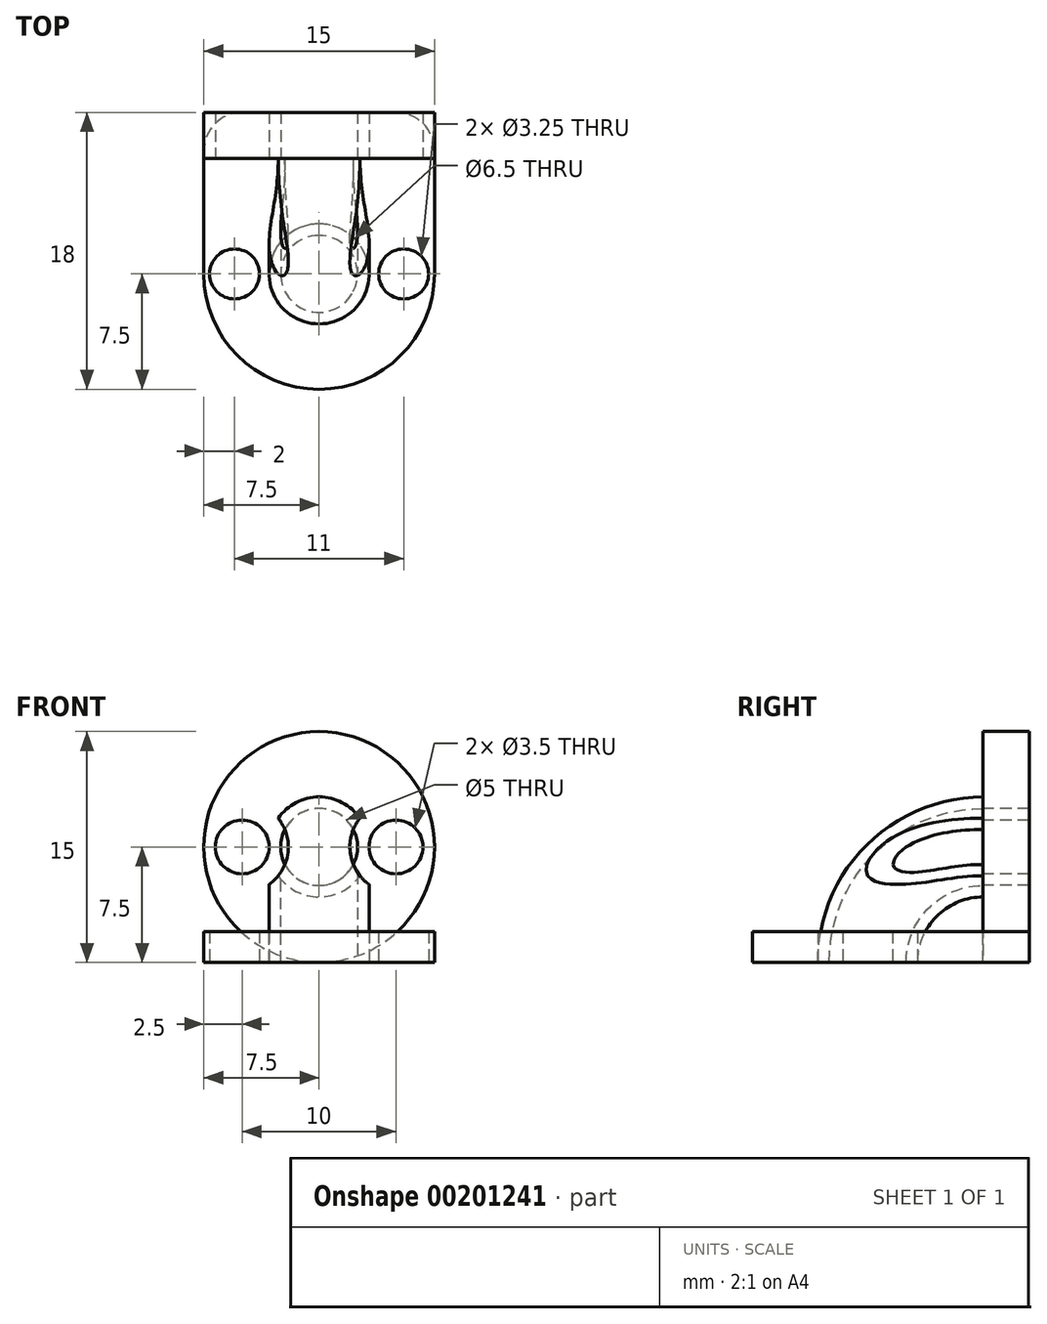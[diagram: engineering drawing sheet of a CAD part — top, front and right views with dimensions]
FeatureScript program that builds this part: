
annotation { "Feature Type Name" : "Feature", "Feature Type Description" : "" }
export const myFeature = defineFeature(function(context is Context, id is Id, definition is map)
    precondition{}
    {
        {
            var Q0;
            Q0=qCreatedBy(makeId("Front.planeOp"),FACE);
            var sketch = newSketch(context, id + "F0", { "sketchPlane" : qUnion([Q0])});
            skCircle(sketch, "E0", {"center": v(0, 0) * mm, "radius": 7.5 * mm});
            skCircle(sketch, "E1", {"center": v(0, 0) * mm, "radius": 2.5 * mm});
            skSolve(sketch);
        }
        {
            var Q0;
            Q0=qSketchRegion(id+"F0",true);
            extrude(context, id + "F1", {"entities" : qUnion([Q0]), "oppositeDirection" : true, "depth" : 3 * mm});
        }
        {
            var Q0;
            Q0=makeQuery(id+"F1.opExtrude","CAP_FACE",FACE,{"disambiguationData":[OSD([sQuery(id+"F0.wireOp",EDGE,"E0"),sQuery(id+"F0.wireOp",EDGE,"E1")])],"isStart":true});
            var sketch = newSketch(context, id + "F2", { "sketchPlane" : qUnion([Q0])});
            skPoint(sketch, "E2", {"position": v(5, 0) * mm});
            skPoint(sketch, "E3", {"position": v(-5, 0) * mm});
            skCircle(sketch, "E4", {"center": v(5, 0) * mm, "radius": 1.75 * mm});
            skCircle(sketch, "E5", {"center": v(-5, 0) * mm, "radius": 1.75 * mm});
            skSolve(sketch);
        }
        {
            var Q0;
            Q0=qSketchRegion(id+"F2",true);
            extrude(context, id + "F3", {"entities" : qUnion([Q0]), "operationType" : NewBodyOperationType.REMOVE, "oppositeDirection" : true, "depth" : 25 * mm});
        }
        {
            var Q0;
            Q0=qCreatedBy(makeId("Right.planeOp"),FACE);
            var sketch = newSketch(context, id + "F4", { "sketchPlane" : qUnion([Q0])});
            skPoint(sketch, "E6", {"position": v(0, -7.5) * mm});
            skArc(sketch, "E7", {"start": v(0, 0) * mm, "mid": v(-5.3, -2.2) * mm, "end": v(-7.5, -7.5) * mm});
            skSolve(sketch);
        }
        {
            var Q0;
            Q0=qCreatedBy(makeId("Front.planeOp"),FACE);
            var sketch = newSketch(context, id + "F5", { "sketchPlane" : qUnion([Q0])});
            skCircle(sketch, "E8", {"center": v(0, 0) * mm, "radius": 2.5 * mm});
            skPoint(sketch, "E9", {"position": v(-3.25, 0) * mm});
            skPoint(sketch, "E10", {"position": v(3.25, 0) * mm});
            skCircle(sketch, "E11", {"center": v(0, 0) * mm, "radius": 3.25 * mm});
            skSolve(sketch);
        }
        {
            var Q0;
            Q0=makeQuery(id+"F5.imprint","IMPRINT",FACE,{"disambiguationData":[TD([[makeQuery(id+"F5.imprint","IMPRINT",EDGE,{"derivedFrom":sQuery(id+"F5.wireOp",EDGE,"E8")}),-1.0]])]});
            var Q1;
            Q1 = qConstructionFilter(qBodyType(qCreatedBy(id + "F4" ,EDGE), BodyType.WIRE), ConstructionObject.NO);
            sweep(context, id + "F6", {"profiles" : qUnion([Q0]), "path" : qUnion([Q1])});
        }
        {
            var Q0;
            Q0=makeQuery(id+"F6.opSweep","CAP_FACE",FACE,{"disambiguationData":[OSD([sQuery(id+"F4.wireOp",VERTEX,"E7.end"),sQuery(id+"F5.wireOp",EDGE,"E8"),sQuery(id+"F5.wireOp",EDGE,"E11")])],"isStart":false});
            var sketch = newSketch(context, id + "F7", { "sketchPlane" : qUnion([Q0])});
            skPoint(sketch, "E12", {"position": v(0, 7.5) * mm});
            skCircle(sketch, "E13", {"center": v(0, 7.5) * mm, "radius": 2.5 * mm});
            skCircle(sketch, "E14", {"center": v(0, 7.5) * mm, "radius": 7.5 * mm});
            skPoint(sketch, "E15", {"position": v(-7.5, 7.5) * mm});
            skPoint(sketch, "E16", {"position": v(7.5, 7.5) * mm});
            skPoint(sketch, "E17", {"position": v(-7.5, -3) * mm});
            skLineSegment(sketch, "E18.bottom", {"start": v(-7.5, -3) * mm, "end": v(7.5, -3) * mm});
            skLineSegment(sketch, "E18.top", {"start": v(-7.5, 7.5) * mm, "end": v(7.5, 7.5) * mm});
            skLineSegment(sketch, "E18.left", {"start": v(-7.5, -3) * mm, "end": v(-7.5, 7.5) * mm});
            skLineSegment(sketch, "E18.right", {"start": v(7.5, -3) * mm, "end": v(7.5, 7.5) * mm});
            skSolve(sketch);
        }
        {
            var Q0;
            Q0=makeQuery(id+"F7.imprint","IMPRINT",FACE,{"disambiguationData":[TD([[makeQuery(id+"F7.imprint","IMPRINT",EDGE,{"derivedFrom":sQuery(id+"F7.wireOp",EDGE,"E14")}),1.0]])]});
            var Q1;
            Q1=makeQuery(id+"F7.imprint","IMPRINT",FACE,{"disambiguationData":[TD([[makeQuery(id+"F7.imprint","IMPRINT",EDGE,{"derivedFrom":sQuery(id+"F7.wireOp",EDGE,"E18.bottom")}),1.0]])]});
            extrude(context, id + "F8", {"entities" : qUnion([Q0, Q1]), "oppositeDirection" : true, "depth" : 2 * mm});
        }
        {
            var Q0;
            Q0=makeQuery(id+"F8.opExtrude","SWEPT_EDGE",EDGE,{"disambiguationData":[OSD([sQuery(id+"F7.wireOp",EDGE,"E18.bottom"),sQuery(id+"F7.wireOp",EDGE,"E18.left")])]});
            var Q1;
            Q1=makeQuery(id+"F8.opExtrude","SWEPT_EDGE",EDGE,{"disambiguationData":[OSD([sQuery(id+"F7.wireOp",EDGE,"E18.bottom"),sQuery(id+"F7.wireOp",EDGE,"E18.right")])]});
            fillet(context, id + "F9", {"entities" : qUnion([Q0, Q1]), "radius" : 2.5 * mm, "tangentPropagation" : true, "allowEdgeOverflow" : false});
        }
        {
            var Q0;
            Q0=makeQuery(id+"F8.opExtrude","CAP_FACE",FACE,{"disambiguationData":[OSD([sQuery(id+"F4.wireOp",VERTEX,"E7.end"),sQuery(id+"F5.wireOp",EDGE,"E11"),sQuery(id+"F7.wireOp",EDGE,"E14"),sQuery(id+"F7.wireOp",EDGE,"E18.bottom"),sQuery(id+"F7.wireOp",EDGE,"E18.left"),sQuery(id+"F7.wireOp",EDGE,"E18.right")])],"isStart":true});
            var sketch = newSketch(context, id + "F10", { "sketchPlane" : qUnion([Q0])});
            skPoint(sketch, "E19", {"position": v(3.78, 3.5) * mm});
            skPoint(sketch, "E20", {"position": v(0, 13) * mm});
            skPoint(sketch, "E21", {"position": v(0, 7.5) * mm});
            skCircle(sketch, "E22", {"center": v(0, 13) * mm, "radius": 1.5 * mm});
            skPoint(sketch, "E23", {"position": v(0, 2) * mm});
            skCircle(sketch, "E24", {"center": v(0, 2) * mm, "radius": 1.5 * mm});
            skPoint(sketch, "E25", {"position": v(-5.5, 7.5) * mm});
            skPoint(sketch, "E26", {"position": v(5.5, 7.5) * mm});
            skCircle(sketch, "E27", {"center": v(-5.5, 7.5) * mm, "radius": 1.63 * mm});
            skCircle(sketch, "E28", {"center": v(5.5, 7.5) * mm, "radius": 1.63 * mm});
            skSolve(sketch);
        }
        {
            var Q0;
            Q0=makeQuery(id+"F10.imprint","IMPRINT",FACE,{"disambiguationData":[TD([[makeQuery(id+"F10.imprint","IMPRINT",EDGE,{"derivedFrom":sQuery(id+"F10.wireOp",EDGE,"E27")}),1.0]])]});
            var Q1;
            Q1=makeQuery(id+"F10.imprint","IMPRINT",FACE,{"disambiguationData":[TD([[makeQuery(id+"F10.imprint","IMPRINT",EDGE,{"derivedFrom":sQuery(id+"F10.wireOp",EDGE,"E28")}),1.0]])]});
            var Q2;
            Q2=makeQuery(id+"F8.opExtrude","CAP_FACE",FACE,{"disambiguationData":[OSD([sQuery(id+"F4.wireOp",VERTEX,"E7.end"),sQuery(id+"F5.wireOp",EDGE,"E11"),sQuery(id+"F7.wireOp",EDGE,"E14"),sQuery(id+"F7.wireOp",EDGE,"E18.bottom"),sQuery(id+"F7.wireOp",EDGE,"E18.left"),sQuery(id+"F7.wireOp",EDGE,"E18.right")])],"isStart":false});
            extrude(context, id + "F11", {"entities" : qUnion([Q0, Q1]), "operationType" : NewBodyOperationType.REMOVE, "endBound" : BoundingType.UP_TO_SURFACE, "oppositeDirection" : true, "endBoundEntityFace" : qUnion([Q2]), "depth" : 25 * mm});
        }
        {
            var Q0;
            Q0=makeQuery(id+"F1.opExtrude","CAP_FACE",FACE,{"disambiguationData":[OSD([sQuery(id+"F0.wireOp",EDGE,"E0"),sQuery(id+"F0.wireOp",EDGE,"E1")])],"isStart":true});
            var sketch = newSketch(context, id + "F12", { "sketchPlane" : qUnion([Q0])});
            skPoint(sketch, "E29", {"position": v(-5, 0) * mm});
            skPoint(sketch, "E30", {"position": v(5, 0) * mm});
            skCircle(sketch, "E31", {"center": v(-5, 0) * mm, "radius": 3 * mm});
            skCircle(sketch, "E32", {"center": v(5, 0) * mm, "radius": 3 * mm});
            skSolve(sketch);
        }
        {
            var Q0;
            Q0 = qSketchRegion(id + "F12", true);
            extrude(context, id + "F13", {"entities" : qUnion([Q0]), "operationType" : NewBodyOperationType.REMOVE, "depth" : 25 * mm});
        }
    });
